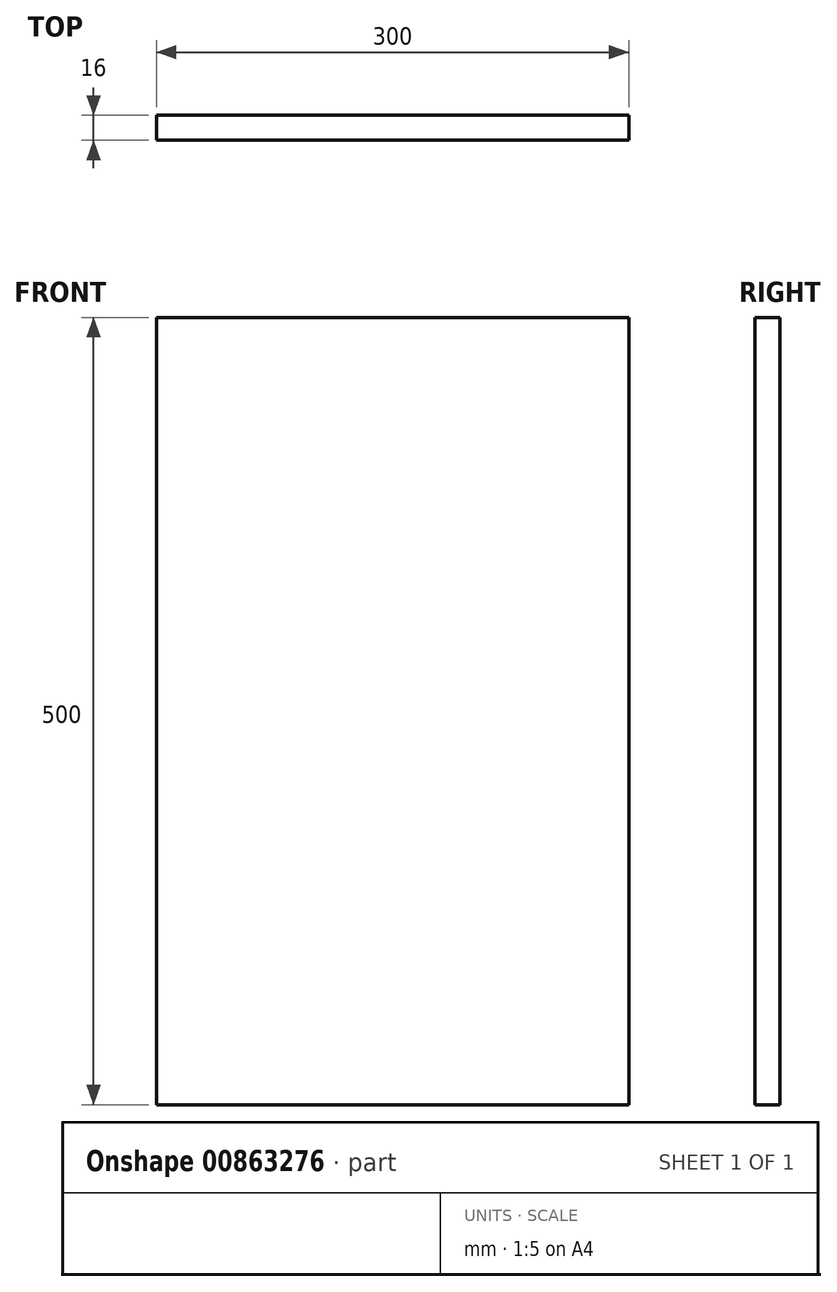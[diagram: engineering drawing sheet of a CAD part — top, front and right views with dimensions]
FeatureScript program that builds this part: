
annotation { "Feature Type Name" : "Feature", "Feature Type Description" : "" }
export const myFeature = defineFeature(function(context is Context, id is Id, definition is map)
    precondition{}
    {
        {
            var Q0;
            Q0=qCreatedBy(makeId("Top.planeOp"),FACE);
            var sketch = newSketch(context, id + "F0", { "sketchPlane" : qUnion([Q0])});
            skLineSegment(sketch, "E0.bottom", {"start": v(0, 0) * mm, "end": v(300, 0) * mm});
            skLineSegment(sketch, "E0.top", {"start": v(0, 16) * mm, "end": v(300, 16) * mm});
            skLineSegment(sketch, "E0.left", {"start": v(0, 0) * mm, "end": v(0, 16) * mm});
            skLineSegment(sketch, "E0.right", {"start": v(300, 0) * mm, "end": v(300, 16) * mm});
            skSolve(sketch);
        }
        {
            var Q0;
            Q0 = qSketchRegion(id + "F0", true);
            extrude(context, id + "F1", {"entities" : qUnion([Q0]), "depth" : 500 * mm, "offsetDistance" : 25 * mm});
        }
    });
